# Revit family: Скамейка стальная «Поло» без спинки Арт 9472
name_source: partatom
category: Антураж
revit_build: Autodesk Revit 2018 (Build: 20180423_1000(x64)
units: mm (PartAtom-declared; Revit-internal decimal feet)

## family parameters
Всегда вертикально = Да
Источник визуального образа = Геометрия семейства
На основе рабочей плоскости = Нет
Общий = Нет
При загрузке вырезать с полостями = Нет
Точка расчета площади = Нет

## types (2) — shared parameters
URL = https://hobbyka.ru
Артикул товара = Арт. 9472
Высота = 400 мм
Группа модели = Скамейки
Изготовитель = ООО «Хоббика»
Изображение типоразмера = Скамейка стальная «Поло» без спинки Арт 9472.jpg
Материал изделия = Сталь, дерево
Цвет лавки = Дерево
Цвет опор = Сталь
Ширина = 385 мм

## per-type parameters (varying)
| type | Версия 1,2 м | Версия 1,8 м | Длина | Кол-во реек | Описание |
| Версия 1,2 м | Да | Нет | 1200 мм | 18 | Скамейка стальная «Поло» без спинки. Версия 1,2 м |
| Версия 1,8 м | Нет | Да | 1800 мм | 27 | Скамейка стальная «Поло» без спинки. Версия 1,8 м |
